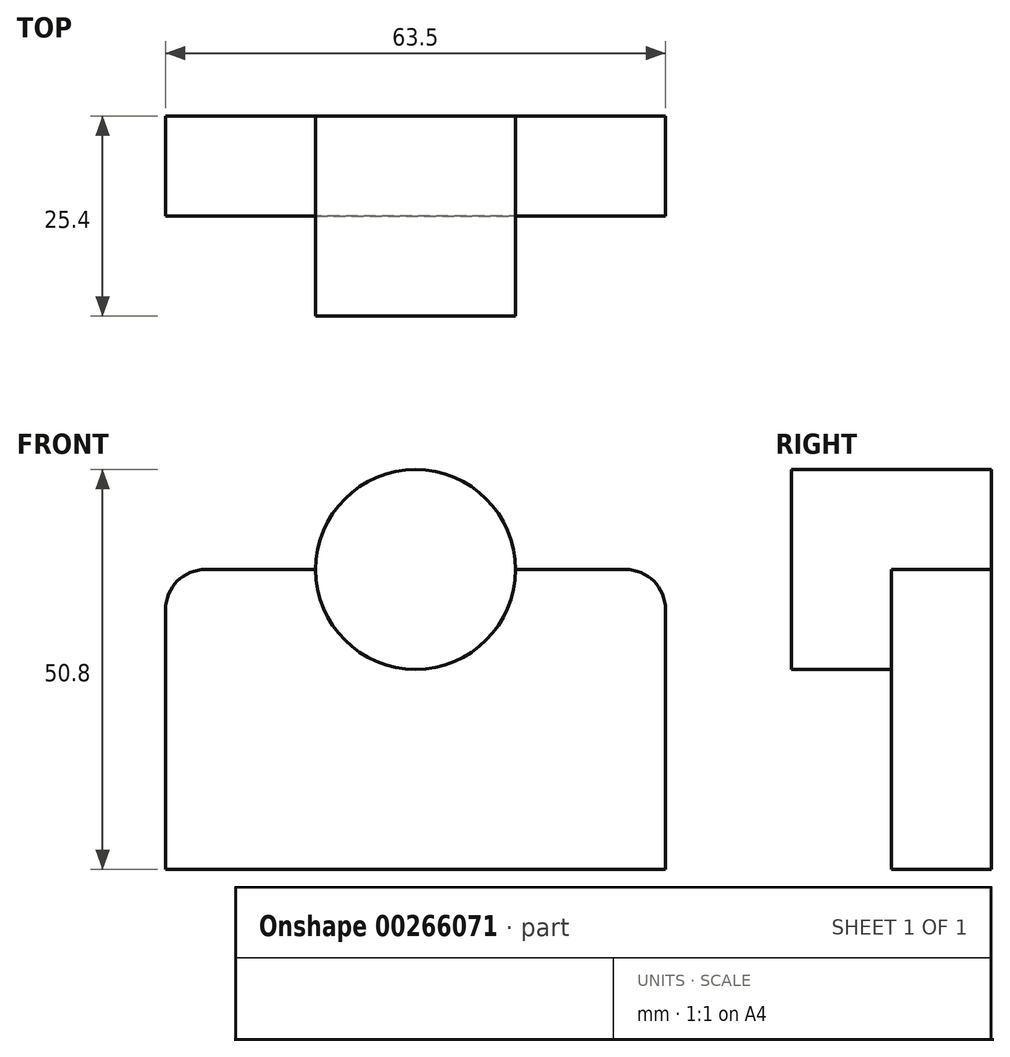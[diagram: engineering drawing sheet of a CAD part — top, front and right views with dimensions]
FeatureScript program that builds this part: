
annotation { "Feature Type Name" : "Feature", "Feature Type Description" : "" }
export const myFeature = defineFeature(function(context is Context, id is Id, definition is map)
    precondition{}
    {
        {
            var Q0;
            Q0=qCreatedBy(makeId("Front.planeOp"),FACE);
            var sketch = newSketch(context, id + "F0", { "sketchPlane" : qUnion([Q0])});
            skLineSegment(sketch, "E0.bottom", {"start": v(31.75, 19.05) * mm, "end": v(-31.75, 19.05) * mm});
            skLineSegment(sketch, "E0.top", {"start": v(31.75, -19.05) * mm, "end": v(-31.75, -19.05) * mm});
            skLineSegment(sketch, "E0.left", {"start": v(31.75, 19.05) * mm, "end": v(31.75, -19.05) * mm});
            skLineSegment(sketch, "E0.right", {"start": v(-31.75, 19.05) * mm, "end": v(-31.75, -19.05) * mm});
            skPoint(sketch, "E0.middle", {"position": v(0, 0) * mm});
            skSolve(sketch);
        }
        {
            var Q0;
            Q0 = qSketchRegion(id + "F0", true);
            extrude(context, id + "F1", {"entities" : qUnion([Q0]), "depth" : 12.7 * mm});
        }
        {
            var Q0;
            Q0=makeQuery(id+"F1.opExtrude","SWEPT_EDGE",EDGE,{"disambiguationData":[OSD([sQuery(id+"F0.wireOp",EDGE,"E0.bottom"),sQuery(id+"F0.wireOp",EDGE,"E0.left")])]});
            var Q1;
            Q1=makeQuery(id+"F1.opExtrude","SWEPT_EDGE",EDGE,{"disambiguationData":[OSD([sQuery(id+"F0.wireOp",EDGE,"E0.bottom"),sQuery(id+"F0.wireOp",EDGE,"E0.right")])]});
            fillet(context, id + "F2", {"entities" : qUnion([Q0, Q1]), "radius" : 5.08 * mm, "tangentPropagation" : true, "allowEdgeOverflow" : false});
        }
        {
            var Q0;
            Q0=qCreatedBy(makeId("Front.planeOp"),FACE);
            var sketch = newSketch(context, id + "F3", { "sketchPlane" : qUnion([Q0])});
            skCircle(sketch, "E1", {"center": v(0, 19.05) * mm, "radius": 12.7 * mm});
            skSolve(sketch);
        }
        {
            var Q0;
            Q0=makeQuery(id+"F3.imprint","IMPRINT",FACE,{"disambiguationData":[TD([[makeQuery(id+"F3.imprint","IMPRINT",EDGE,{"derivedFrom":sQuery(id+"F3.wireOp",EDGE,"E1")}),1.0]])]});
            extrude(context, id + "F4", {"entities" : qUnion([Q0]), "operationType" : NewBodyOperationType.ADD, "depth" : 25.4 * mm});
        }
    });
